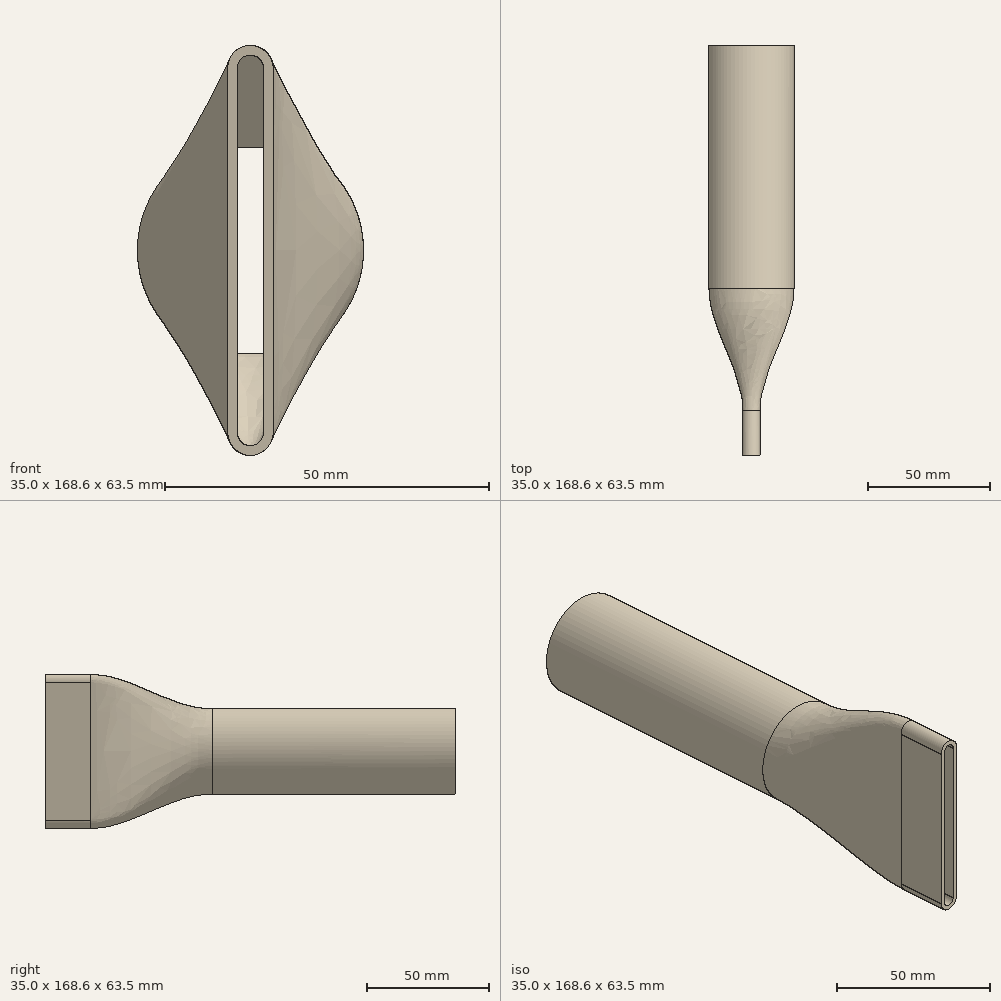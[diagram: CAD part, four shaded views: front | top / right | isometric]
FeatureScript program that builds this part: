
annotation { "Feature Type Name" : "Feature", "Feature Type Description" : "" }
export const myFeature = defineFeature(function(context is Context, id is Id, definition is map)
    precondition{}
    {
        {
            var Q0;
            Q0=qCreatedBy(makeId("Front.planeOp"),FACE);
            var sketch = newSketch(context, id + "F0", { "sketchPlane" : qUnion([Q0])});
            skCircle(sketch, "E0", {"center": v(0, 0) * mm, "radius": 17.5 * mm});
            skSolve(sketch);
        }
        {
            var Q0;
            Q0 = qSketchRegion(id + "F0", true);
            extrude(context, id + "F1", {"entities" : qUnion([Q0]), "depth" : 100 * mm});
        }
        {
            var Q0;
            Q0=makeQuery(id+"F1.opExtrude","CAP_FACE",FACE,{"disambiguationData":[OSD([sQuery(id+"F0.wireOp",EDGE,"E0")])],"isStart":false});
            cPlane(context, id + "F2", {"entities" : qUnion([Q0]), "cplaneType" : CPlaneType.OFFSET, "offset" : 50 * mm, "width" : 150 * mm, "height" : 150 * mm});
        }
        {
            var Q0;
            Q0=qCreatedBy(id+"F2.planeOp",FACE);
            var sketch = newSketch(context, id + "F3", { "sketchPlane" : qUnion([Q0])});
            skLineSegment(sketch, "E1.bottom", {"start": v(3.5, 28.23) * mm, "end": v(-3.5, 28.23) * mm});
            skLineSegment(sketch, "E1.top", {"start": v(3.5, -28.23) * mm, "end": v(-3.5, -28.23) * mm});
            skLineSegment(sketch, "E1.left", {"start": v(3.5, 28.23) * mm, "end": v(3.5, -28.23) * mm});
            skLineSegment(sketch, "E1.right", {"start": v(-3.5, 28.23) * mm, "end": v(-3.5, -28.23) * mm});
            skPoint(sketch, "E1.middle", {"position": v(0, 0) * mm});
            skArc(sketch, "E2", {"start": v(3.5, 28.23) * mm, "mid": v(0, 31.73) * mm, "end": v(-3.5, 28.23) * mm});
            skArc(sketch, "E3", {"start": v(-3.5, -28.23) * mm, "mid": v(0, -31.73) * mm, "end": v(3.5, -28.23) * mm});
            skSolve(sketch);
        }
        {
            var Q0;
            Q0 = qSketchRegion(id + "F3", true);
            extrude(context, id + "F4", {"entities" : qUnion([Q0]), "depth" : 25 * mm});
        }
        {
            var Q0;
            Q0=makeQuery(id+"F1.opExtrude","CAP_FACE",FACE,{"disambiguationData":[OSD([sQuery(id+"F0.wireOp",EDGE,"E0")])],"isStart":false});
            var sketch = newSketch(context, id + "F5", { "sketchPlane" : qUnion([Q0])});
            skLineSegment(sketch, "E4", {"start": v(12.37, 12.37) * mm, "end": v(-12.37, -12.37) * mm, "construction": true});
            skLineSegment(sketch, "E5", {"start": v(12.37, -12.37) * mm, "end": v(-12.37, 12.37) * mm, "construction": true});
            skArc(sketch, "E6", {"start": v(12.37, 12.37) * mm, "mid": v(0, 17.5) * mm, "end": v(-12.37, 12.37) * mm});
            skArc(sketch, "E7", {"start": v(12.37, -12.37) * mm, "mid": v(17.5, 0) * mm, "end": v(12.37, 12.37) * mm});
            skArc(sketch, "E8", {"start": v(-12.37, -12.37) * mm, "mid": v(0, -17.5) * mm, "end": v(12.37, -12.37) * mm});
            skArc(sketch, "E9", {"start": v(-12.37, 12.37) * mm, "mid": v(-17.5, 0) * mm, "end": v(-12.37, -12.37) * mm});
            skSolve(sketch);
        }
        {
            var Q0;
            Q0 = qSketchRegion(id + "F5", true);
            var Q1;
            Q1=makeQuery(id+"F4.opExtrude","CAP_FACE",FACE,{"disambiguationData":[OSD([sQuery(id+"F3.wireOp",EDGE,"E1.left"),sQuery(id+"F3.wireOp",EDGE,"E1.right"),sQuery(id+"F3.wireOp",EDGE,"E2"),sQuery(id+"F3.wireOp",EDGE,"E3")])],"isStart":true});
            loft(context, id + "F6", {"operationType" : NewBodyOperationType.ADD, "startCondition" : LoftEndDerivativeType.NORMAL_TO_PROFILE, "startMagnitude" : 1, "endCondition" : LoftEndDerivativeType.NORMAL_TO_PROFILE, "endMagnitude" : 1, "sheetProfilesArray" : [{ "sheetProfileEntities" : qUnion([Q0]) }, { "sheetProfileEntities" : qUnion([Q1]) }]});
        }
        {
            var Q0;
            Q0=makeQuery(id+"F1.opExtrude","CAP_FACE",FACE,{"disambiguationData":[OSD([sQuery(id+"F0.wireOp",EDGE,"E0")])],"isStart":true});
            shell(context, id + "F7", {"entities" : qUnion([Q0]), "thickness" : 1.5 * mm});
        }
        {
            var Q0;
            Q0=makeQuery(id+"F4.opExtrude","SWEPT_FACE",FACE,{"disambiguationData":[OSD([sQuery(id+"F3.wireOp",EDGE,"E1.left")])]});
            var sketch = newSketch(context, id + "F8", { "sketchPlane" : qUnion([Q0])});
            skLineSegment(sketch, "E10.bottom", {"start": v(-181.44, 39.53) * mm, "end": v(-168.56, 39.53) * mm});
            skLineSegment(sketch, "E10.top", {"start": v(-181.44, -39.53) * mm, "end": v(-168.56, -39.53) * mm});
            skLineSegment(sketch, "E10.left", {"start": v(-181.44, 39.53) * mm, "end": v(-181.44, -39.53) * mm});
            skLineSegment(sketch, "E10.right", {"start": v(-168.56, 39.53) * mm, "end": v(-168.56, -39.53) * mm});
            skPoint(sketch, "E10.middle", {"position": v(-175, 0) * mm});
            skSolve(sketch);
        }
        {
            var Q0;
            Q0 = qSketchRegion(id + "F8", true);
            extrude(context, id + "F9", {"entities" : qUnion([Q0]), "operationType" : NewBodyOperationType.REMOVE, "oppositeDirection" : true, "depth" : 25 * mm});
        }
    });
